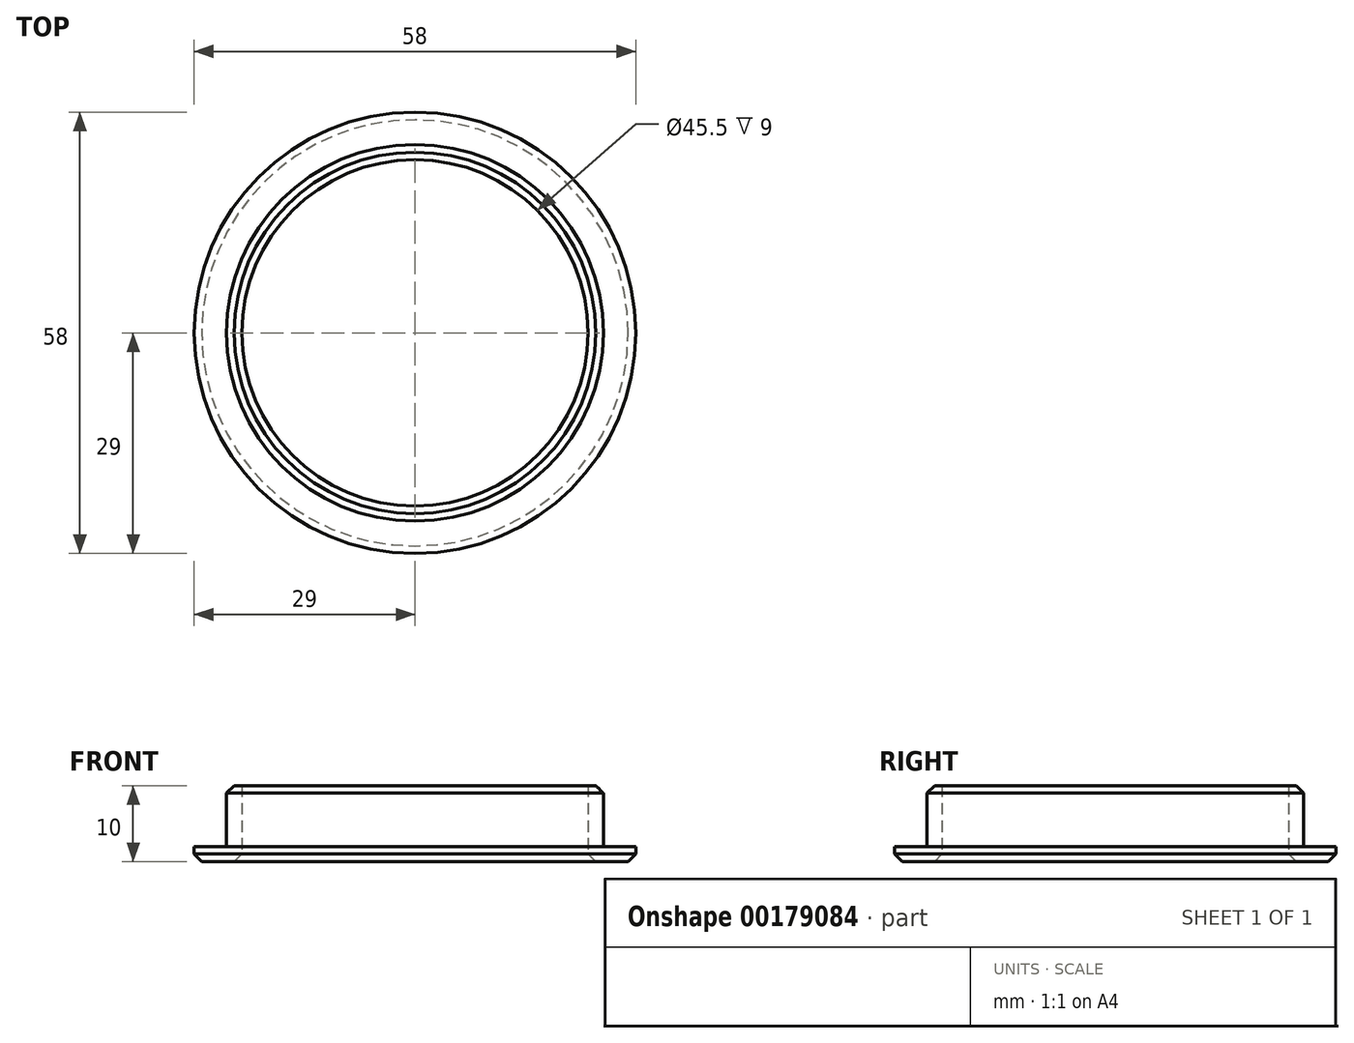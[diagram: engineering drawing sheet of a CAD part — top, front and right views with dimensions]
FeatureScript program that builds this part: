
annotation { "Feature Type Name" : "Feature", "Feature Type Description" : "" }
export const myFeature = defineFeature(function(context is Context, id is Id, definition is map)
    precondition{}
    {
        {
            var Q0;
            Q0=qCreatedBy(makeId("Top.planeOp"),FACE);
            var sketch = newSketch(context, id + "F0", { "sketchPlane" : qUnion([Q0])});
            skCircle(sketch, "E0", {"center": v(0, 0) * mm, "radius": 24.75 * mm});
            skCircle(sketch, "E1", {"center": v(0, 0) * mm, "radius": 22.75 * mm});
            skSolve(sketch);
        }
        {
            var Q0;
            Q0=makeQuery(id+"F0.imprint","IMPRINT",FACE,{"disambiguationData":[TD([[makeQuery(id+"F0.imprint","IMPRINT",EDGE,{"derivedFrom":sQuery(id+"F0.wireOp",EDGE,"E0")}),1.0]])]});
            extrude(context, id + "F1", {"entities" : qUnion([Q0]), "depth" : 10 * mm});
        }
        {
            var Q0;
            Q0=qCreatedBy(makeId("Top.planeOp"),FACE);
            var sketch = newSketch(context, id + "F2", { "sketchPlane" : qUnion([Q0])});
            skCircle(sketch, "E2", {"center": v(0, 0) * mm, "radius": 29 * mm});
            skCircle(sketch, "E3", {"center": v(0, 0) * mm, "radius": 22.75 * mm});
            skSolve(sketch);
        }
        {
            var Q0;
            Q0=makeQuery(id+"F2.imprint","IMPRINT",FACE,{"disambiguationData":[TD([[makeQuery(id+"F2.imprint","IMPRINT",EDGE,{"derivedFrom":sQuery(id+"F2.wireOp",EDGE,"E2")}),1.0]])]});
            extrude(context, id + "F3", {"entities" : qUnion([Q0]), "operationType" : NewBodyOperationType.ADD, "depth" : 2 * mm});
        }
        {
            var Q0;
            Q0=makeQuery(id+"F3.opExtrude","CAP_EDGE",EDGE,{"disambiguationData":[OSD([sQuery(id+"F2.wireOp",EDGE,"E2")])],"isStart":true});
            var Q1;
            Q1=makeQuery(id+"F1.opExtrude","CAP_EDGE",EDGE,{"disambiguationData":[OSD([sQuery(id+"F0.wireOp",EDGE,"E1")])],"isStart":true});
            var Q2;
            Q2=makeQuery(id+"F1.opExtrude","CAP_EDGE",EDGE,{"disambiguationData":[OSD([sQuery(id+"F0.wireOp",EDGE,"E0")])],"isStart":false});
            chamfer(context, id + "F4", {"entities" : qUnion([Q0, Q1, Q2]), "width" : 1 * mm, "tangentPropagation" : true});
        }
    });
